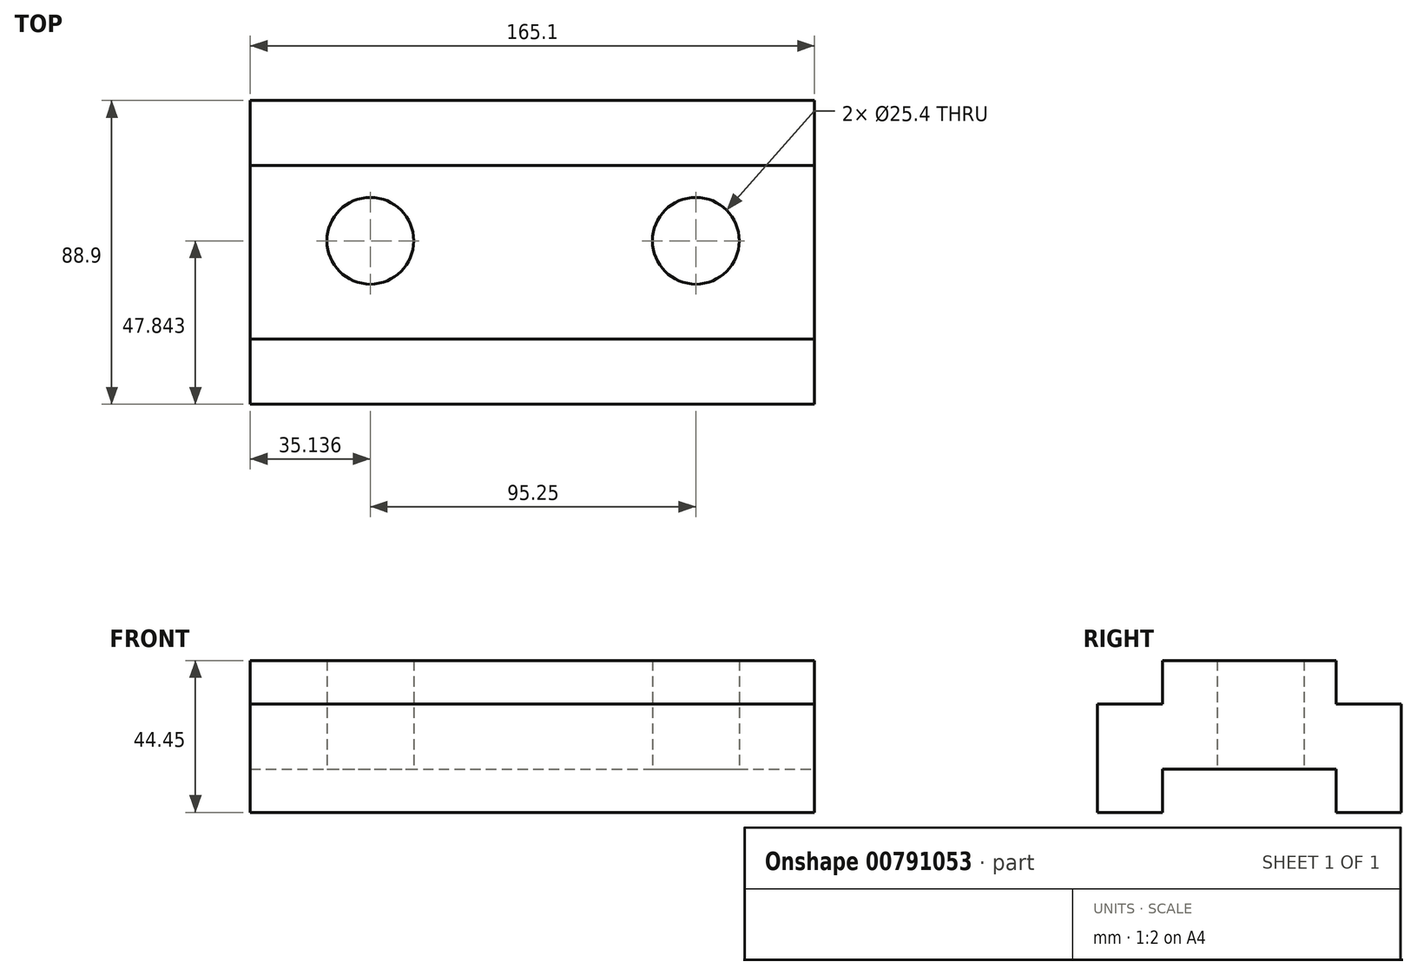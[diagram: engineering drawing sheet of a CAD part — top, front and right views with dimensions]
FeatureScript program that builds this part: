
annotation { "Feature Type Name" : "Feature", "Feature Type Description" : "" }
export const myFeature = defineFeature(function(context is Context, id is Id, definition is map)
    precondition{}
    {
        {
            var Q0;
            Q0=qCreatedBy(makeId("Right.planeOp"),FACE);
            var sketch = newSketch(context, id + "F0", { "sketchPlane" : qUnion([Q0])});
            skLineSegment(sketch, "E0", {"start": v(0, 0) * mm, "end": v(19.05, 0) * mm});
            skLineSegment(sketch, "E1", {"start": v(19.05, 0) * mm, "end": v(19.05, 12.7) * mm});
            skLineSegment(sketch, "E2", {"start": v(19.05, 12.7) * mm, "end": v(69.85, 12.7) * mm});
            skLineSegment(sketch, "E3", {"start": v(69.85, 12.7) * mm, "end": v(69.85, 0) * mm});
            skLineSegment(sketch, "E4", {"start": v(69.85, 0) * mm, "end": v(88.9, 0) * mm});
            skLineSegment(sketch, "E5", {"start": v(88.9, 0) * mm, "end": v(88.9, 31.75) * mm});
            skLineSegment(sketch, "E6", {"start": v(88.9, 31.75) * mm, "end": v(69.85, 31.75) * mm});
            skLineSegment(sketch, "E7", {"start": v(69.85, 31.75) * mm, "end": v(69.85, 44.45) * mm});
            skLineSegment(sketch, "E8", {"start": v(69.85, 44.45) * mm, "end": v(19.05, 44.45) * mm});
            skLineSegment(sketch, "E9", {"start": v(19.05, 44.45) * mm, "end": v(19.05, 31.75) * mm});
            skLineSegment(sketch, "E10", {"start": v(19.05, 31.75) * mm, "end": v(0, 31.75) * mm});
            skLineSegment(sketch, "E11", {"start": v(0, 31.75) * mm, "end": v(0, 0) * mm});
            skSolve(sketch);
        }
        {
            var Q0;
            Q0=makeQuery(id+"F0.imprint","IMPRINT",FACE,{"disambiguationData":[TD([[makeQuery(id+"F0.imprint","IMPRINT",EDGE,{"derivedFrom":sQuery(id+"F0.wireOp",EDGE,"E0")}),1.0]])]});
            extrude(context, id + "F1", {"entities" : qUnion([Q0]), "oppositeDirection" : true, "depth" : 165.1 * mm, "offsetDistance" : 25.4 * mm});
        }
        {
            var Q0;
            Q0=qCreatedBy(makeId("Top.planeOp"),FACE);
            var sketch = newSketch(context, id + "F2", { "sketchPlane" : qUnion([Q0])});
            skLineSegment(sketch, "E12", {"start": v(-164.89, 47.84) * mm, "end": v(-129.96, 47.84) * mm, "construction": true});
            skLineSegment(sketch, "E13", {"start": v(-129.96, 47.84) * mm, "end": v(-34.71, 47.84) * mm, "construction": true});
            skCircle(sketch, "E14", {"center": v(-129.96, 47.84) * mm, "radius": 12.7 * mm});
            skCircle(sketch, "E15", {"center": v(-34.71, 47.84) * mm, "radius": 12.7 * mm});
            skSolve(sketch);
        }
        {
            var Q0;
            Q0=makeQuery(id+"F2.imprint","IMPRINT",FACE,{"disambiguationData":[TD([[makeQuery(id+"F2.imprint","IMPRINT",EDGE,{"derivedFrom":sQuery(id+"F2.wireOp",EDGE,"E14")}),1.0]])]});
            var Q1;
            Q1=makeQuery(id+"F2.imprint","IMPRINT",FACE,{"disambiguationData":[TD([[makeQuery(id+"F2.imprint","IMPRINT",EDGE,{"derivedFrom":sQuery(id+"F2.wireOp",EDGE,"E15")}),1.0]])]});
            extrude(context, id + "F3", {"entities" : qUnion([Q0, Q1]), "operationType" : NewBodyOperationType.REMOVE, "endBound" : BoundingType.THROUGH_ALL, "depth" : 25.4 * mm, "offsetDistance" : 25.4 * mm});
        }
    });
